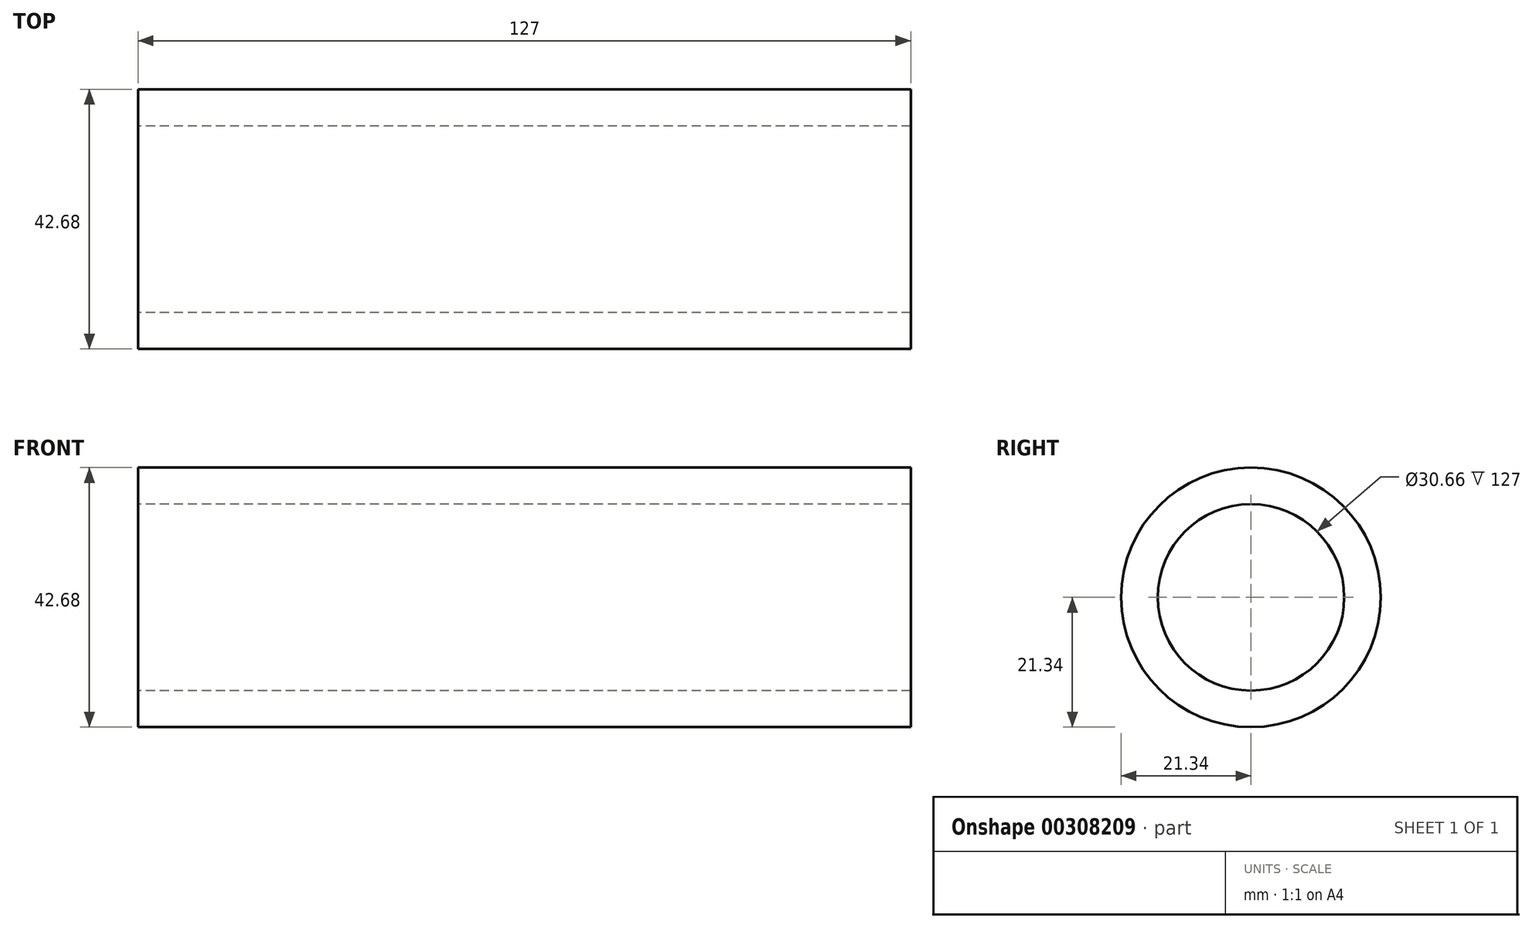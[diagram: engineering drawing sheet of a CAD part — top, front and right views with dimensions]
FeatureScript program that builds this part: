
annotation { "Feature Type Name" : "Feature", "Feature Type Description" : "" }
export const myFeature = defineFeature(function(context is Context, id is Id, definition is map)
    precondition{}
    {
        {
            var Q0;
            Q0=qCreatedBy(makeId("Right.planeOp"),FACE);
            var sketch = newSketch(context, id + "F0", { "sketchPlane" : qUnion([Q0])});
            skCircle(sketch, "E0", {"center": v(0, 0) * mm, "radius": 15.33 * mm});
            skCircle(sketch, "E1", {"center": v(0, 0) * mm, "radius": 21.34 * mm});
            skSolve(sketch);
        }
        {
            var Q0;
            Q0 = qSketchRegion(id + "F0", true);
            extrude(context, id + "F1", {"entities" : qUnion([Q0]), "endBound" : BoundingType.SYMMETRIC, "depth" : 127 * mm});
        }
    });
